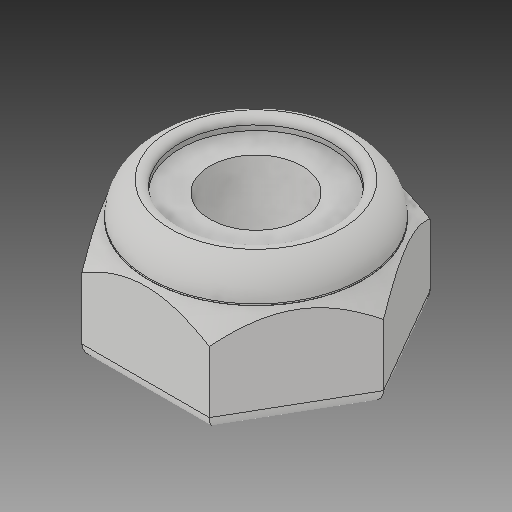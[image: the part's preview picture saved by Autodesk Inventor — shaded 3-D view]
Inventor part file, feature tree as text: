
AUTODESK INVENTOR PART (.ipt)
format: ipt  version: 2017 (Build 210142000, 142)  size: 161,280 bytes
history: native  units: in
note: dims shown in document units (in); Inventor stores cm internally (conversion verified against a paired STEP export)
features: fillet x1
ambient origin geometry x8: Origin, YZ Plane, XZ Plane, XY Plane, X Axis, Y Axis, Z Axis, Center Point
bodies: Solid1 (feature_tree)
feature tree (1):
  fillet  "Fillet5"  [1 undecoded]
note: 1 required parameter value undecoded (feature->parameter linkage not recoverable at this tier; creation-order binding heuristic only, values carry confidence <= 0.55)
